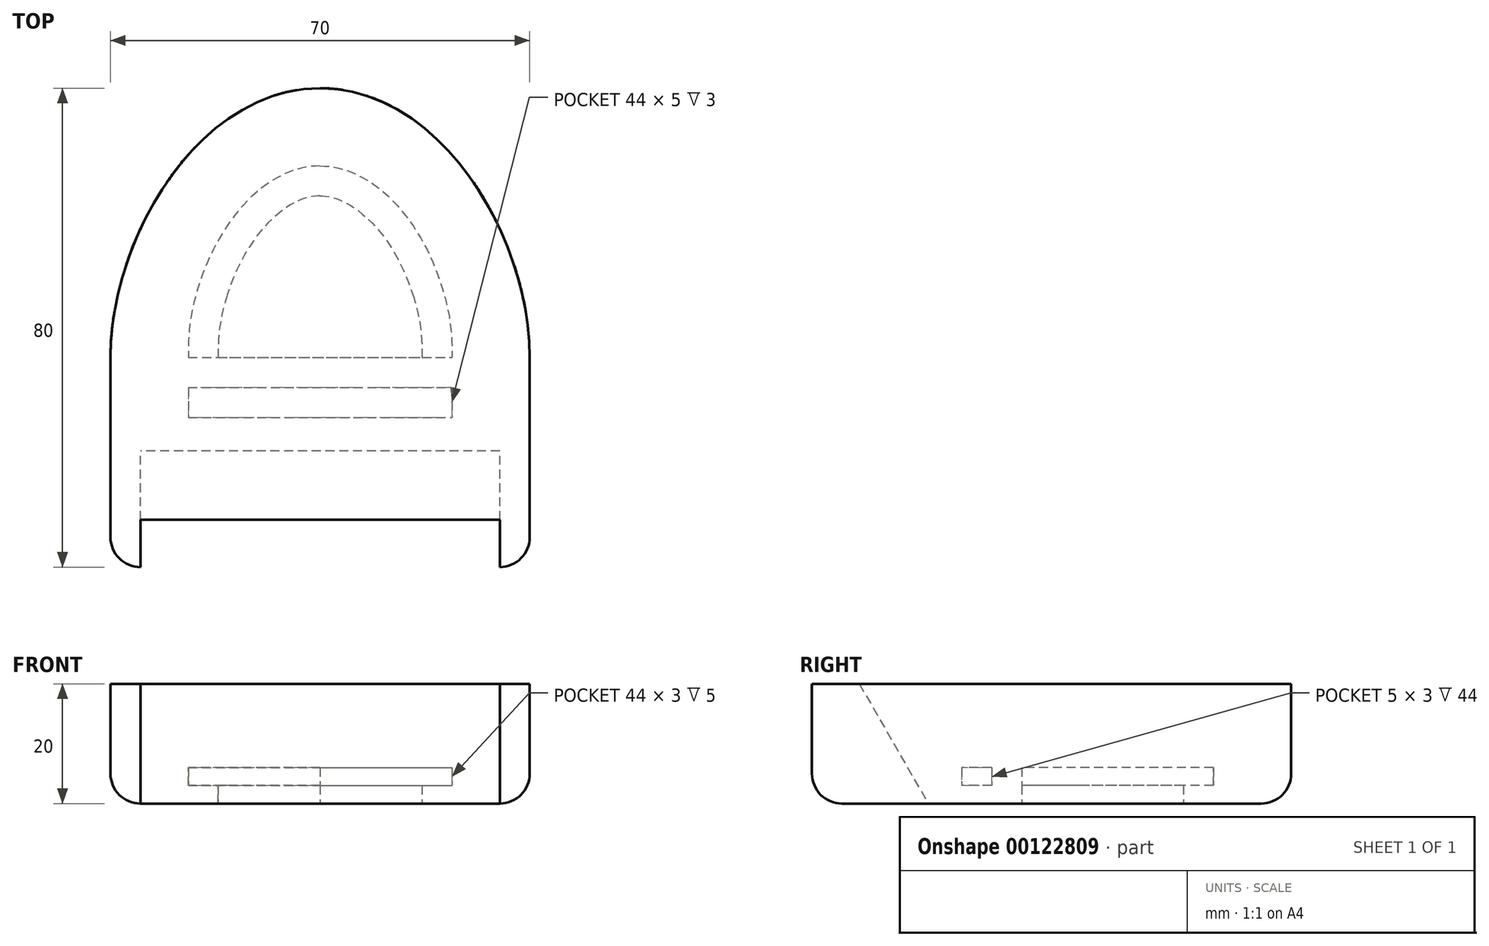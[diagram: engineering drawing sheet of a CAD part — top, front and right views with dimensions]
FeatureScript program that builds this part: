
annotation { "Feature Type Name" : "Feature", "Feature Type Description" : "" }
export const myFeature = defineFeature(function(context is Context, id is Id, definition is map)
    precondition{}
    {
        {
            var Q0;
            Q0=qCreatedBy(makeId("Top.planeOp"),FACE);
            var sketch = newSketch(context, id + "F0", { "sketchPlane" : qUnion([Q0])});
            skLineSegment(sketch, "E0.top", {"start": v(-35, -35) * mm, "end": v(35, -35) * mm});
            skPoint(sketch, "E0.middle", {"position": v(0, 0) * mm});
            skPoint(sketch, "E1.visualSharp", {"position": v(-35, -35) * mm});
            skPoint(sketch, "E2.visualSharp", {"position": v(35, -35) * mm});
            skPoint(sketch, "E3", {"position": v(-35, 0) * mm});
            skPoint(sketch, "E4", {"position": v(35, 5) * mm});
            skLineSegment(sketch, "E5", {"start": v(-35, 0) * mm, "end": v(-35, -35) * mm});
            skLineSegment(sketch, "E6", {"start": v(35, 5) * mm, "end": v(35, -35) * mm});
            skFitSpline(sketch, "E7", {"points": [v(0, 45) * mm, v(-35, 0) * mm], "startDerivative": vector(-60.6, 0) * mm, "endDerivative": vector(0, -60.15) * mm});
            skFitSpline(sketch, "E8.MirrorCS", {"points": [v(0, 45) * mm, v(35, 0) * mm], "startDerivative": vector(60.6, 0) * mm, "endDerivative": vector(0, -60.15) * mm});
            skSolve(sketch);
        }
        {
            var Q0;
            Q0=qSketchRegion(id+"F0",true);
            extrude(context, id + "F1", {"entities" : qUnion([Q0]), "endBound" : BoundingType.SYMMETRIC, "depth" : 25 * mm});
        }
        {
            var Q0;
            Q0=qCreatedBy(makeId("Right.planeOp"),FACE);
            var sketch = newSketch(context, id + "F2", { "sketchPlane" : qUnion([Q0])});
            skLineSegment(sketch, "E9", {"start": v(0, 0) * mm, "end": v(-30, 0) * mm});
            skPoint(sketch, "E10", {"position": v(-30, 0) * mm});
            skLineSegment(sketch, "E11", {"start": v(-30, 12.5) * mm, "end": v(-30, -12.5) * mm});
            skLineSegment(sketch, "E12", {"start": v(-30, -12.5) * mm, "end": v(0, -12.5) * mm});
            skLineSegment(sketch, "E13", {"start": v(-30, 12.5) * mm, "end": v(-15.57, -12.5) * mm});
            skLineSegment(sketch, "E14", {"start": v(-30, 7.5) * mm, "end": v(-27.11, 7.5) * mm});
            skLineSegment(sketch, "E15.bottom", {"start": v(-30, 7.5) * mm, "end": v(-40, 7.5) * mm});
            skLineSegment(sketch, "E15.top", {"start": v(-30, -12.5) * mm, "end": v(-40, -12.5) * mm});
            skLineSegment(sketch, "E15.left", {"start": v(-30, 7.5) * mm, "end": v(-30, -12.5) * mm});
            skLineSegment(sketch, "E15.right", {"start": v(-40, 7.5) * mm, "end": v(-40, -12.5) * mm});
            skSolve(sketch);
        }
        {
            var Q0;
            {var subQ0=sQuery(id+"F2.wireOp",EDGE,"E11");var subQ1=sQuery(id+"F2.wireOp",EDGE,"E9");var subQ2=makeQuery(id+"F2.imprint","INTERSECT",VERTEX,{"derivedFrom":[subQ1,subQ0]});Q0=makeQuery(id+"F2.imprint","IMPRINT",FACE,{"disambiguationData":[TD([[makeQuery(id+"F2.imprint","IMPRINT",EDGE,{"disambiguationData":[TD([[subQ2,1.0]])],"derivedFrom":subQ1}),1.0]])]});}
            var Q1;
            {var subQ0=sQuery(id+"F2.wireOp",EDGE,"E11");var subQ1=sQuery(id+"F2.wireOp",EDGE,"E9");var subQ2=makeQuery(id+"F2.imprint","INTERSECT",VERTEX,{"derivedFrom":[subQ1,subQ0]});Q1=makeQuery(id+"F2.imprint","IMPRINT",FACE,{"disambiguationData":[TD([[makeQuery(id+"F2.imprint","IMPRINT",EDGE,{"disambiguationData":[TD([[subQ2,1.0]])],"derivedFrom":subQ1}),-1.0]])]});}
            var Q2;
            {var subQ4=sQuery(id+"F2.wireOp",EDGE,"8ufA6tNX-FfDE-ZJzA-wNNM-ROf074WZHJ4W.bottom");Q2=makeQuery(id+"F2.imprint","IMPRINT",FACE,{"disambiguationData":[TD([[makeQuery(id+"F2.imprint","IMPRINT",EDGE,{"derivedFrom":subQ4}),1.0]])]});}
            var Q3;
            {var subQ3=sQuery(id+"F2.wireOp",EDGE,"E15.bottom");Q3=makeQuery(id+"F2.imprint","IMPRINT",FACE,{"disambiguationData":[TD([[makeQuery(id+"F2.imprint","IMPRINT",EDGE,{"derivedFrom":subQ3}),1.0]])]});}
            extrude(context, id + "F3", {"entities" : qUnion([Q0, Q1, Q2, Q3]), "operationType" : NewBodyOperationType.REMOVE, "endBound" : BoundingType.SYMMETRIC, "depth" : 60 * mm});
        }
        {
            var Q0;
            Q0=makeQuery(id+"F1.opExtrude","CAP_FACE",FACE,{"disambiguationData":[OSD([sQuery(id+"F0.wireOp",EDGE,"E0.top"),sQuery(id+"F0.wireOp",EDGE,"49a04736-c9a8-4021-8eca-e335ee950ef4"),sQuery(id+"F0.wireOp",EDGE,"5cda4a63-8e27-4d9c-be18-28a9360ed2950.MirrorCS"),sQuery(id+"F0.wireOp",EDGE,"E5"),sQuery(id+"F0.wireOp",EDGE,"E6")])],"isStart":true});
            var sketch = newSketch(context, id + "F4", { "sketchPlane" : qUnion([Q0])});
            skLineSegment(sketch, "E16.bottom", {"start": v(35, 35) * mm, "end": v(-25, 35) * mm});
            skLineSegment(sketch, "E16.top", {"start": v(35, 15.57) * mm, "end": v(-30, 15.57) * mm});
            skLineSegment(sketch, "E16.left", {"start": v(35, 15.57) * mm, "end": v(35, 35) * mm});
            skLineSegment(sketch, "E16.right", {"start": v(-30, 0) * mm, "end": v(-30, 15.57) * mm});
            skFitSpline(sketch, "E17", {"points": [v(0, -40) * mm, v(30, 0) * mm], "startDerivative": vector(49.89, 0) * mm, "endDerivative": vector(0, 60.15) * mm});
            skFitSpline(sketch, "E18.MirrorCS", {"points": [v(0, -40) * mm, v(-30, 0) * mm], "startDerivative": vector(-49.89, 0) * mm, "endDerivative": vector(0, 60.15) * mm});
            skFitSpline(sketch, "E19.0", {"points": [v(0, -32) * mm, v(0.64, -32) * mm, v(1.9, -31.9) * mm, v(3.77, -31.49) * mm, v(5.66, -30.78) * mm, v(8.18, -29.45) * mm, v(11.32, -27.03) * mm, v(14.84, -22.99) * mm, v(17.86, -18) * mm, v(20.18, -12.32) * mm, v(21.66, -6.22) * mm, v(22, -2.06) * mm, v(22, 0) * mm]});
            skFitSpline(sketch, "E19.1", {"points": [v(0, -32) * mm, v(-0.64, -32) * mm, v(-1.9, -31.9) * mm, v(-3.77, -31.49) * mm, v(-5.66, -30.78) * mm, v(-8.18, -29.45) * mm, v(-11.32, -27.03) * mm, v(-14.84, -22.99) * mm, v(-17.86, -18) * mm, v(-20.18, -12.32) * mm, v(-21.66, -6.22) * mm, v(-22, -2.06) * mm, v(-22, 0) * mm]});
            skFitSpline(sketch, "E20.0", {"points": [v(0, -27) * mm, v(0.4, -27) * mm, v(1.15, -26.94) * mm, v(2.33, -26.68) * mm, v(3.59, -26.21) * mm, v(4.94, -25.5) * mm, v(6.36, -24.53) * mm, v(8.32, -22.85) * mm, v(10.76, -20.06) * mm, v(13.36, -15.76) * mm, v(15.4, -10.78) * mm, v(16.7, -5.42) * mm, v(17, -1.78) * mm, v(17, 0) * mm]});
            skFitSpline(sketch, "E20.1", {"points": [v(0, -27) * mm, v(-0.4, -27) * mm, v(-1.15, -26.94) * mm, v(-2.33, -26.68) * mm, v(-3.59, -26.21) * mm, v(-4.94, -25.5) * mm, v(-6.36, -24.53) * mm, v(-8.32, -22.85) * mm, v(-10.76, -20.06) * mm, v(-13.36, -15.76) * mm, v(-15.4, -10.78) * mm, v(-16.7, -5.42) * mm, v(-17, -1.78) * mm, v(-17, 0) * mm]});
            skLineSegment(sketch, "E21.bottom", {"start": v(-22, 0) * mm, "end": v(22, 0) * mm});
            skLineSegment(sketch, "E21.top", {"start": v(-22, 10) * mm, "end": v(22, 10) * mm});
            skLineSegment(sketch, "E21.left", {"start": v(-22, 0) * mm, "end": v(-22, 10) * mm});
            skLineSegment(sketch, "E21.right", {"start": v(22, 0) * mm, "end": v(22, 10) * mm});
            skLineSegment(sketch, "E22", {"start": v(-20.56, -10.51) * mm, "end": v(-15.34, -10.51) * mm});
            skLineSegment(sketch, "E23.MirrorCS", {"start": v(20.56, -10.51) * mm, "end": v(15.34, -10.51) * mm});
            skLineSegment(sketch, "E24.top", {"start": v(-22, 5) * mm, "end": v(22, 5) * mm});
            skLineSegment(sketch, "E24.left", {"start": v(-22, 10) * mm, "end": v(-22, 5) * mm});
            skLineSegment(sketch, "E24.right", {"start": v(22, 10) * mm, "end": v(22, 5) * mm});
            skSolve(sketch);
        }
        {
            var Q0;
            Q0=makeQuery(id+"F4.imprint","IMPRINT",FACE,{"disambiguationData":[TD([[makeQuery(id+"F4.imprint","IMPRINT",EDGE,{"derivedFrom":sQuery(id+"F4.wireOp",EDGE,"E21.top")}),-1.0]])]});
            var Q1;
            {var subQ0=sQuery(id+"F4.wireOp",EDGE,"E21.left");Q1=makeQuery(id+"F4.imprint","IMPRINT",FACE,{"disambiguationData":[TD([[makeQuery(id+"F4.imprint","IMPRINT",EDGE,{"derivedFrom":subQ0}),-1.0]])]});}
            var Q2;
            {var subQ1=sQuery(id+"F4.wireOp",EDGE,"E20.1");var subQ4=sQuery(id+"F4.wireOp",EDGE,"E20.0");var subQ5=makeQuery(id+"F4.imprint","INTERSECT",VERTEX,{"derivedFrom":[subQ4,subQ1]});Q2=makeQuery(id+"F4.imprint","IMPRINT",FACE,{"disambiguationData":[TD([[makeQuery(id+"F4.imprint","IMPRINT",EDGE,{"disambiguationData":[TD([[subQ5,-1.0]])],"derivedFrom":subQ4}),1.0]])]});}
            var Q3;
            {var subQ0=sQuery(id+"F4.wireOp",EDGE,"E21.bottom");var subQ5=sQuery(id+"F4.wireOp",EDGE,"E20.1");var subQ6=makeQuery(id+"F4.imprint","INTERSECT",VERTEX,{"derivedFrom":[subQ5,subQ0]});Q3=makeQuery(id+"F4.imprint","IMPRINT",FACE,{"disambiguationData":[TD([[makeQuery(id+"F4.imprint","IMPRINT",EDGE,{"disambiguationData":[TD([[subQ6,1.0]])],"derivedFrom":subQ5}),1.0]])]});}
            var Q4;
            {var subQ5=sQuery(id+"F4.wireOp",EDGE,"E19.1");var subQ9=sQuery(id+"F4.wireOp",EDGE,"E19.0");var subQ10=makeQuery(id+"F4.imprint","INTERSECT",VERTEX,{"derivedFrom":[subQ9,subQ5]});Q4=makeQuery(id+"F4.imprint","IMPRINT",FACE,{"disambiguationData":[TD([[makeQuery(id+"F4.imprint","IMPRINT",EDGE,{"disambiguationData":[TD([[subQ10,-1.0]])],"derivedFrom":subQ9}),1.0]])]});}
            var Q5;
            {var subQ0=sQuery(id+"F4.wireOp",EDGE,"E21.bottom");var subQ5=sQuery(id+"F4.wireOp",EDGE,"E20.0");var subQ6=makeQuery(id+"F4.imprint","INTERSECT",VERTEX,{"derivedFrom":[subQ5,subQ0]});Q5=makeQuery(id+"F4.imprint","IMPRINT",FACE,{"disambiguationData":[TD([[makeQuery(id+"F4.imprint","IMPRINT",EDGE,{"disambiguationData":[TD([[subQ6,1.0]])],"derivedFrom":subQ5}),-1.0]])]});}
            extrude(context, id + "F5", {"entities" : qUnion([Q0, Q1, Q2, Q3, Q4, Q5]), "operationType" : NewBodyOperationType.REMOVE, "oppositeDirection" : true, "depth" : 6 * mm});
        }
        {
            var Q0;
            {var subQ5=sQuery(id+"F4.wireOp",EDGE,"E19.1");var subQ9=sQuery(id+"F4.wireOp",EDGE,"E19.0");var subQ10=makeQuery(id+"F4.imprint","INTERSECT",VERTEX,{"derivedFrom":[subQ9,subQ5]});Q0=makeQuery(id+"F4.imprint","IMPRINT",FACE,{"disambiguationData":[TD([[makeQuery(id+"F4.imprint","IMPRINT",EDGE,{"disambiguationData":[TD([[subQ10,-1.0]])],"derivedFrom":subQ9}),1.0]])]});}
            var Q1;
            Q1=makeQuery(id+"F4.imprint","IMPRINT",FACE,{"disambiguationData":[TD([[makeQuery(id+"F4.imprint","IMPRINT",EDGE,{"derivedFrom":sQuery(id+"F4.wireOp",EDGE,"E21.top")}),-1.0]])]});
            extrude(context, id + "F6", {"entities" : qUnion([Q0, Q1]), "operationType" : NewBodyOperationType.ADD, "oppositeDirection" : true, "depth" : 3 * mm});
        }
        {
            var Q0;
            Q0=makeQuery(id+"F1.opExtrude","CAP_EDGE",EDGE,{"disambiguationData":[OSD([sQuery(id+"F0.wireOp",EDGE,"E5")])],"isStart":true});
            var Q1;
            Q1=makeQuery(id+"F1.opExtrude","CAP_EDGE",EDGE,{"disambiguationData":[OSD([sQuery(id+"F0.wireOp",EDGE,"E7")])],"isStart":true});
            var Q2;
            Q2=makeQuery(id+"F1.opExtrude","CAP_EDGE",EDGE,{"disambiguationData":[OSD([sQuery(id+"F0.wireOp",EDGE,"E0.top")])],"isStart":false});
            var Q3;
            Q3=makeQuery(id+"F1.opExtrude","CAP_EDGE",EDGE,{"disambiguationData":[OSD([sQuery(id+"F0.wireOp",EDGE,"E5")])],"isStart":false});
            var Q4;
            Q4=makeQuery(id+"F1.opExtrude","SWEPT_EDGE",EDGE,{"disambiguationData":[OSD([sQuery(id+"F0.wireOp",EDGE,"E0.top"),sQuery(id+"F0.wireOp",EDGE,"E5")])]});
            var Q5;
            Q5=makeQuery(id+"F1.opExtrude","SWEPT_EDGE",EDGE,{"disambiguationData":[OSD([sQuery(id+"F0.wireOp",EDGE,"E0.top"),sQuery(id+"F0.wireOp",EDGE,"E6")])]});
            var Q6;
            {var subQ0=sQuery(id+"F0.wireOp",EDGE,"E0.top");var subQ1=sQuery(id+"F0.wireOp",EDGE,"E5");Q6=makeQuery(id+"F3.boolean.opBoolean","SPLIT",EDGE,{"disambiguationData":[TD([makeQuery(id+"F1.opExtrude","SWEPT_FACE",FACE,{"disambiguationData":[OSD([subQ1])]})])],"derivedFrom":makeQuery(id+"F1.opExtrude","CAP_EDGE",EDGE,{"disambiguationData":[OSD([subQ0])],"isStart":true})});}
            var Q7;
            {var subQ0=sQuery(id+"F0.wireOp",EDGE,"E0.top");var subQ1=sQuery(id+"F0.wireOp",EDGE,"E6");Q7=makeQuery(id+"F3.boolean.opBoolean","SPLIT",EDGE,{"disambiguationData":[TD([makeQuery(id+"F1.opExtrude","SWEPT_FACE",FACE,{"disambiguationData":[OSD([subQ1])]})])],"derivedFrom":makeQuery(id+"F1.opExtrude","CAP_EDGE",EDGE,{"disambiguationData":[OSD([subQ0])],"isStart":true})});}
            fillet(context, id + "F7", {"entities" : qUnion([Q0, Q1, Q2, Q3, Q4, Q5, Q6, Q7]), "radius" : 5 * mm, "tangentPropagation" : true, "allowEdgeOverflow" : false});
        }
        {
            var Q0;
            Q0=makeQuery(id+"F1.opExtrude","CAP_FACE",FACE,{"disambiguationData":[OSD([sQuery(id+"F0.wireOp",EDGE,"E0.top"),sQuery(id+"F0.wireOp",EDGE,"E5"),sQuery(id+"F0.wireOp",EDGE,"E6"),sQuery(id+"F0.wireOp",EDGE,"E7"),sQuery(id+"F0.wireOp",EDGE,"E8.MirrorCS")])],"isStart":false});
            var sketch = newSketch(context, id + "F8", { "sketchPlane" : qUnion([Q0])});
            skLineSegment(sketch, "E25.bottom", {"start": v(-46.34, 47) * mm, "end": v(46.34, 47) * mm});
            skLineSegment(sketch, "E25.top", {"start": v(-46.34, -47) * mm, "end": v(46.34, -47) * mm});
            skLineSegment(sketch, "E25.left", {"start": v(-46.34, 47) * mm, "end": v(-46.34, -47) * mm});
            skLineSegment(sketch, "E25.right", {"start": v(46.34, 47) * mm, "end": v(46.34, -47) * mm});
            skPoint(sketch, "E25.middle", {"position": v(0, 0) * mm});
            skSolve(sketch);
        }
        {
            var Q0;
            Q0 = qSketchRegion(id + "F8", true);
            extrude(context, id + "F9", {"entities" : qUnion([Q0]), "operationType" : NewBodyOperationType.REMOVE, "oppositeDirection" : true, "depth" : 5 * mm});
        }
    });
